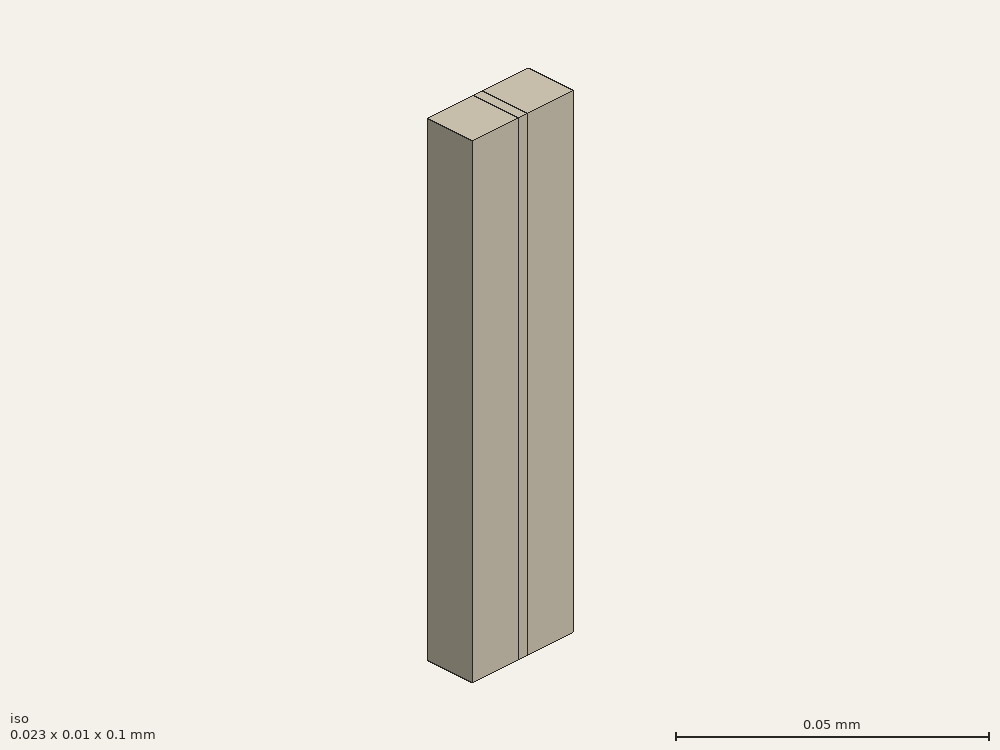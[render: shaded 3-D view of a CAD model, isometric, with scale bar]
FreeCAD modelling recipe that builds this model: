
FCSTD DOCUMENT  (FreeCAD 0.21R33694 (Git))
Label: straight-loaded
License: All rights reserved
LicenseURL: http://en.wikipedia.org/wiki/All_rights_reserved
objects: Part::Part2DObjectPython×6, App::FeaturePython×4, Part::Extrusion×2, Part::FeaturePython×2
note: 10 computed .brp shape members not serialized (recipe doc carries the construction recipe); baked Part::Feature solids carry a one-line shape summary decoded from their .brp

FEATURE [Part::Part2DObjectPython] Rectangle  # Draft 2D object (typed FeaturePython)
  Area = 232.258
  ChamferSize = 0
  Columns = 1
  FilletRadius = 0
  Height = 10.16
  Length = 22.86
  MakeFace = true
  Placement = pos=(-11.43,-5.08,0) rot=(0,0,1;0rad)
  Rows = 1
FEATURE [Part::Part2DObjectPython] Rectangle001  label="_Pport1"  # Draft 2D object (typed FeaturePython)
  Area = 0.000232258
  ChamferSize = 0
  Columns = 1
  FilletRadius = 0
  Height = 0.01016
  Length = 0.02286
  MakeFace = true
  Placement = pos=(-0.01143,-0.00508,0.1) rot=(0,0,1;0rad)
  Rows = 1
FEATURE [Part::Part2DObjectPython] Line  label="_Pv1"  # Draft 2D object (typed FeaturePython)
  Area = 0
  ChamferSize = 0
  Closed = false
  End = (-1.8e-15,0.00508,0.1)
  FilletRadius = 0
  Length = 0.01016
  MakeFace = true
  Placement = pos=(0,-0.00508,0.1) rot=(0,0,1;0rad)
  Points = (2) [(0,0,0),(-1.77605e-15,0.01016,0)]
  Start = (0,-0.00508,0.1)
  Subdivisions = 0
FEATURE [Part::Part2DObjectPython] Rectangle002  label="_Pport2"  # Draft 2D object (typed FeaturePython)
  Area = 0.000232258
  ChamferSize = 0
  Columns = 1
  FilletRadius = 0
  Height = 0.01016
  Length = 0.02286
  MakeFace = true
  Placement = pos=(-0.01143,-0.00508,0) rot=(0,0,1;0rad)
  Rows = 1
FEATURE [Part::Part2DObjectPython] Line001  label="_Pv2"  # Draft 2D object (typed FeaturePython)
  Area = 0
  ChamferSize = 0
  Closed = false
  End = (0,0.00508,0)
  FilletRadius = 0
  Length = 0.01016
  MakeFace = true
  Placement = pos=(0,-0.00508,0) rot=(0,0,1;0rad)
  Points = (2) [(0,0,0),(3.1106e-19,0.01016,0)]
  Start = (0,-0.00508,0)
  Subdivisions = 0
FEATURE [App::FeaturePython] Text  label="_Sinput(PV){port1}"  # WARN: FeaturePython — macro-defined, semantics opaque (R4)
  Placement = pos=(0.0413747,-0.017509,0) rot=(0,0,1;0rad)
  Text = .
FEATURE [App::FeaturePython] Text001  label="_Soutput(PV){port2}"  # WARN: FeaturePython — macro-defined, semantics opaque (R4)
  Placement = pos=(0.0413747,-0.017509,0) rot=(0,0,1;0rad)
  Text = .
FEATURE [App::FeaturePython] Text002  label="_Linput(1,voltage){v1}"  # WARN: FeaturePython — macro-defined, semantics opaque (R4)
  Placement = pos=(0.0413747,-0.017509,0) rot=(0,0,1;0rad)
  Text = .
FEATURE [App::FeaturePython] Text003  label="_Loutput(2,voltage){v2}"  # WARN: FeaturePython — macro-defined, semantics opaque (R4)
  Placement = pos=(0.0413747,-0.017509,0) rot=(0,0,1;0rad)
  Text = .
FEATURE [Part::Extrusion] Extrude
  Base = -> Rectangle
  Dir = (0,0,1)
  DirMode = 2
  FaceMakerClass = Part::FaceMakerBullseye
  LengthFwd = 100
  LengthRev = 0
  Solid = false
  Symmetric = false
FEATURE [Part::Part2DObjectPython] Rectangle004  # Draft 2D object (typed FeaturePython)
  Area = 20.32
  ChamferSize = 0
  Columns = 1
  FilletRadius = 0
  Height = 2
  Length = 10.16
  MakeFace = true
  Placement = pos=(-1,-5.08,0) rot=(0.707107,0.707107,0;3.14159rad)
  Rows = 1
FEATURE [Part::Extrusion] Extrude001
  Base = -> Rectangle004
  Dir = (1e-16,-1e-16,-1)
  DirMode = 2
  FaceMakerClass = Part::FaceMakerBullseye
  LengthFwd = -100
  LengthRev = 0
  Solid = false
  Symmetric = false
FEATURE [Part::FeaturePython] BooleanFragments  # WARN: FeaturePython — macro-defined, semantics opaque (R4)
  Mode = 0
  Objects = -> [Extrude,Extrude001]
  Tolerance = 0
FEATURE [Part::FeaturePython] Clone  label="scaled"  # Draft clone (typed FeaturePython)
  AttacherType = Attacher::AttachEngine3D
  Fuse = false
  Objects = -> [BooleanFragments]
  Scale = (0.001,0.001,0.001)
